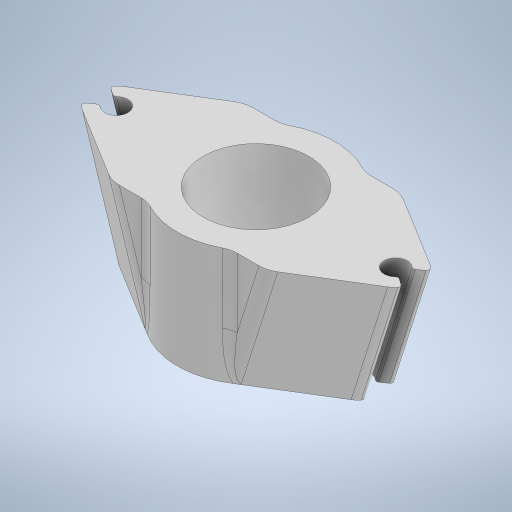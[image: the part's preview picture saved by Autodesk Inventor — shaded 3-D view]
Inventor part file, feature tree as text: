
AUTODESK INVENTOR PART (.ipt)
format: ipt  version: 2023 (Build 270158000, 158)  size: 389,120 bytes
history: native  units: in
note: dims shown in document units (in); Inventor stores cm internally (conversion verified against a paired STEP export)
features: sketch x3, sweep x2, extrude x2, fillet x2, projected_geometry x1
ambient origin geometry x8: Origin, YZ Plane, XZ Plane, XY Plane, X Axis, Y Axis, Z Axis, Center Point
bodies: Body1 (feature_tree)
feature tree (10):
  sketch  "Sketch5"  dims[d48=0.61in d54=0.45in]
  sketch  "Sketch1"  dims[d21=0.2405in d22=0.2405in]
  sweep  "Sweep1"
  sweep  "Sweep2"
  extrude  "Extrusion4"  Depth=0.1in
  extrude  "Extrusion5"  Depth=0.1in
  fillet  "Fillet3"  [1 undecoded]
  fillet  "Fillet4"  [1 undecoded]
  sketch  "Sketch7"  dims[d55=0.1202in d56=0.2405in d57=0.1202in d58=0.0in d59=0.0in d60=0.0in d61=0.0in d64=0.45in d65=0.0in d66=0.41in d67=0.4in d68=0.0in d69=0.01in d70=0.1in d15=0.0in d16=0.0in d17=0.0in d18=0.0in]
  projected_geometry  "Projected Loop4"
note: 2 required parameter values undecoded (feature->parameter linkage not recoverable at this tier; creation-order binding heuristic only, values carry confidence <= 0.55)
